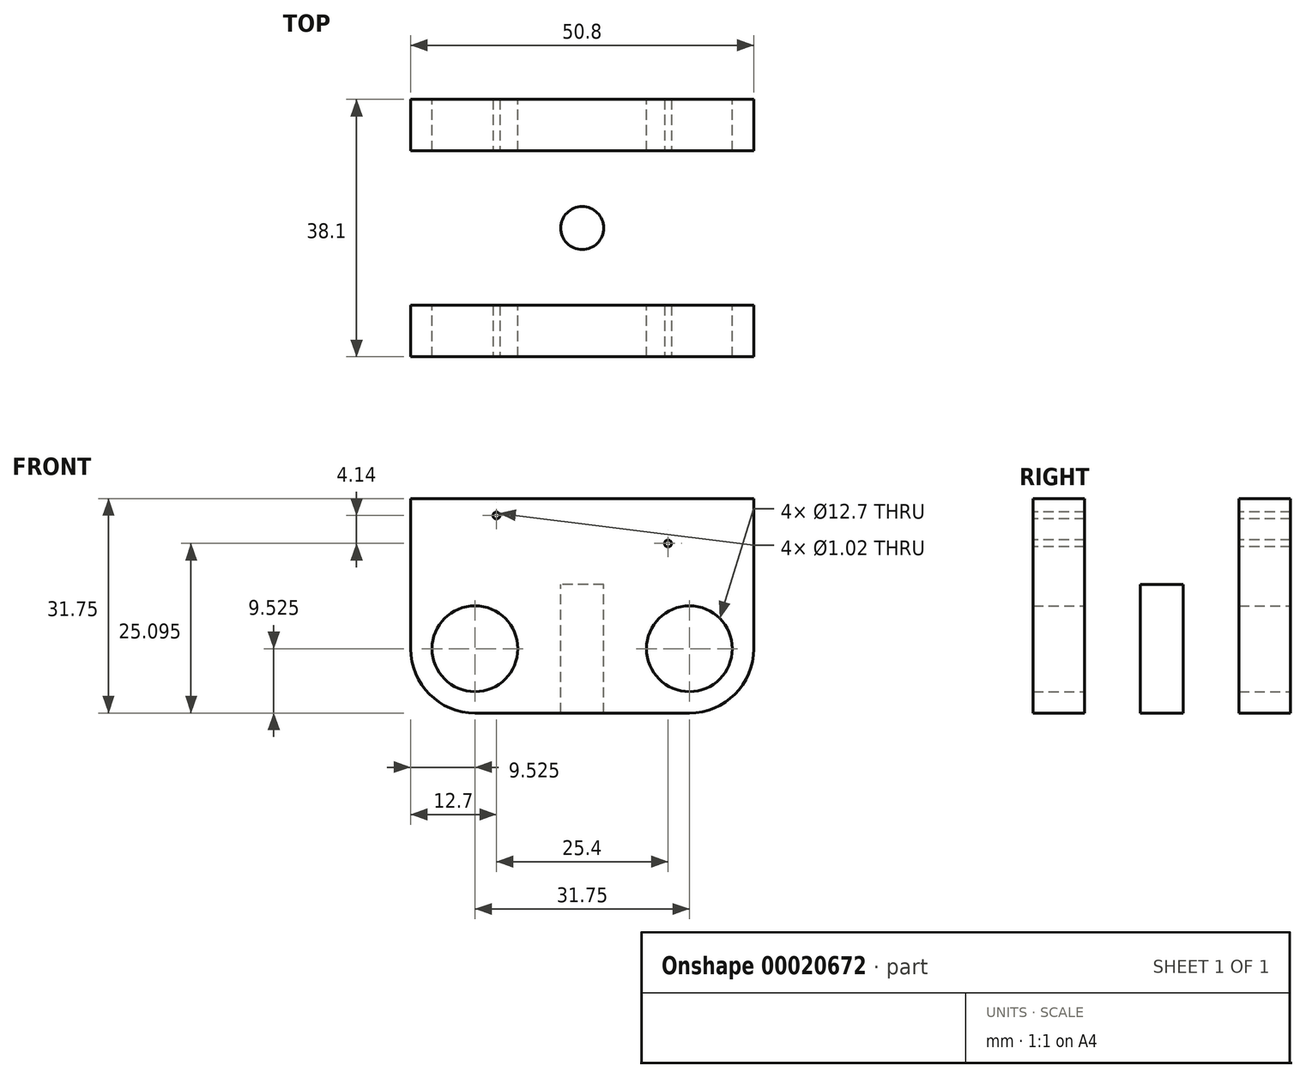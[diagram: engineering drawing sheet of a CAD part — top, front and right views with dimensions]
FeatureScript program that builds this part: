
annotation { "Feature Type Name" : "Feature", "Feature Type Description" : "" }
export const myFeature = defineFeature(function(context is Context, id is Id, definition is map)
    precondition{}
    {
        {
            var Q0;
            Q0=qCreatedBy(makeId("Front.planeOp"),FACE);
            var sketch = newSketch(context, id + "F0", { "sketchPlane" : qUnion([Q0])});
            skLineSegment(sketch, "E0.bottom", {"start": v(0, 0) * mm, "end": v(50.8, 0) * mm});
            skLineSegment(sketch, "E0.top", {"start": v(0, 19.05) * mm, "end": v(50.8, 19.05) * mm});
            skLineSegment(sketch, "E0.left", {"start": v(0, 0) * mm, "end": v(0, 19.05) * mm});
            skLineSegment(sketch, "E0.right", {"start": v(50.8, 0) * mm, "end": v(50.8, 19.05) * mm});
            skCircle(sketch, "E1", {"center": v(41.28, 9.52) * mm, "radius": 6.35 * mm});
            skCircle(sketch, "E2", {"center": v(9.53, 9.52) * mm, "radius": 6.35 * mm});
            skLineSegment(sketch, "E3", {"start": v(0, 9.52) * mm, "end": v(50.8, 9.52) * mm});
            skSolve(sketch);
        }
        {
            var Q0;
            {var subQ11=sQuery(id+"F0.wireOp",EDGE,"E0.top");Q0=makeQuery(id+"F0.imprint","IMPRINT",FACE,{"disambiguationData":[TD([[makeQuery(id+"F0.imprint","IMPRINT",EDGE,{"derivedFrom":subQ11}),-1.0]])]});}
            var Q1;
            {var subQ11=sQuery(id+"F0.wireOp",EDGE,"E0.bottom");Q1=makeQuery(id+"F0.imprint","IMPRINT",FACE,{"disambiguationData":[TD([[makeQuery(id+"F0.imprint","IMPRINT",EDGE,{"derivedFrom":subQ11}),1.0]])]});}
            extrude(context, id + "F1", {"entities" : qUnion([Q0, Q1]), "depth" : 38.1 * mm});
        }
        {
            var Q0;
            Q0=makeQuery(id+"F1.opExtrude","SWEPT_FACE",FACE,{"disambiguationData":[OSD([sQuery(id+"F0.wireOp",EDGE,"E0.top")])]});
            var sketch = newSketch(context, id + "F2", { "sketchPlane" : qUnion([Q0])});
            skLineSegment(sketch, "E4", {"start": v(25.4, -38.1) * mm, "end": v(25.4, 0) * mm});
            skCircle(sketch, "E5", {"center": v(25.4, -19.05) * mm, "radius": 3.18 * mm});
            skLineSegment(sketch, "E6.bottom", {"start": v(0, -30.48) * mm, "end": v(50.8, -30.48) * mm});
            skLineSegment(sketch, "E6.top", {"start": v(0, -38.1) * mm, "end": v(50.8, -38.1) * mm});
            skLineSegment(sketch, "E6.left", {"start": v(0, -30.48) * mm, "end": v(0, -38.1) * mm});
            skLineSegment(sketch, "E6.right", {"start": v(50.8, -30.48) * mm, "end": v(50.8, -38.1) * mm});
            skLineSegment(sketch, "E7", {"start": v(25.4, -19.05) * mm, "end": v(16.8, -19.05) * mm, "construction": true});
            skLineSegment(sketch, "E8.MirrorCS", {"start": v(50.8, -7.62) * mm, "end": v(50.8, 0) * mm});
            skLineSegment(sketch, "E9.MirrorCS", {"start": v(0, 0) * mm, "end": v(50.8, 0) * mm});
            skLineSegment(sketch, "E10.MirrorCS", {"start": v(0, -7.62) * mm, "end": v(0, 0) * mm});
            skLineSegment(sketch, "E11.MirrorCS", {"start": v(0, -7.62) * mm, "end": v(50.8, -7.62) * mm});
            skSolve(sketch);
        }
        {
            var Q0;
            {var subQ0=sQuery(id+"F2.wireOp",EDGE,"E5");var subQ1=sQuery(id+"F2.wireOp",EDGE,"E4");var subQ3=makeQuery(id+"F2.imprint","INTERSECT",VERTEX,{"disambiguationData":[OD(0.0)],"derivedFrom":[subQ1,subQ0]});Q0=makeQuery(id+"F2.imprint","IMPRINT",FACE,{"disambiguationData":[TD([[makeQuery(id+"F2.imprint","IMPRINT",EDGE,{"disambiguationData":[TD([[subQ3,-1.0]])],"derivedFrom":subQ1}),-1.0]])]});}
            var Q1;
            {var subQ0=sQuery(id+"F2.wireOp",EDGE,"E5");var subQ1=sQuery(id+"F2.wireOp",EDGE,"E4");var subQ3=makeQuery(id+"F2.imprint","INTERSECT",VERTEX,{"disambiguationData":[OD(0.0)],"derivedFrom":[subQ1,subQ0]});Q1=makeQuery(id+"F2.imprint","IMPRINT",FACE,{"disambiguationData":[TD([[makeQuery(id+"F2.imprint","IMPRINT",EDGE,{"disambiguationData":[TD([[subQ3,-1.0]])],"derivedFrom":subQ1}),1.0]])]});}
            var Q2;
            Q2=sQuery(id+"F2.wireOp",EDGE,"E5");
            extrude(context, id + "F3", {"entities" : qUnion([Q0, Q1]), "operationType" : NewBodyOperationType.REMOVE, "surfaceEntities" : qUnion([Q2]), "endBound" : BoundingType.THROUGH_ALL, "oppositeDirection" : true, "depth" : 25.4 * mm});
        }
        {
            var Q0;
            {var subQ0=sQuery(id+"F2.wireOp",EDGE,"E6.left");Q0=makeQuery(id+"F2.imprint","IMPRINT",FACE,{"disambiguationData":[TD([[makeQuery(id+"F2.imprint","IMPRINT",EDGE,{"derivedFrom":subQ0}),-1.0]])]});}
            var Q1;
            {var subQ0=sQuery(id+"F2.wireOp",EDGE,"E6.right");Q1=makeQuery(id+"F2.imprint","IMPRINT",FACE,{"disambiguationData":[TD([[makeQuery(id+"F2.imprint","IMPRINT",EDGE,{"derivedFrom":subQ0}),1.0]])]});}
            var Q2;
            {var subQ3=sQuery(id+"F2.wireOp",EDGE,"E10.MirrorCS");Q2=makeQuery(id+"F2.imprint","IMPRINT",FACE,{"disambiguationData":[TD([[makeQuery(id+"F2.imprint","IMPRINT",EDGE,{"derivedFrom":subQ3}),-1.0]])]});}
            var Q3;
            {var subQ3=sQuery(id+"F2.wireOp",EDGE,"E8.MirrorCS");Q3=makeQuery(id+"F2.imprint","IMPRINT",FACE,{"disambiguationData":[TD([[makeQuery(id+"F2.imprint","IMPRINT",EDGE,{"derivedFrom":subQ3}),1.0]])]});}
            extrude(context, id + "F4", {"entities" : qUnion([Q0, Q1, Q2, Q3]), "operationType" : NewBodyOperationType.ADD, "depth" : 12.7 * mm});
        }
        {
            var Q0;
            Q0=makeQuery(id+"F4.boolean.opBoolean","MERGE",FACE,{"derivedFrom":[makeQuery(id+"F1.opExtrude","CAP_FACE",FACE,{"disambiguationData":[OSD([sQuery(id+"F0.wireOp",EDGE,"E0.bottom"),sQuery(id+"F0.wireOp",EDGE,"E0.top"),sQuery(id+"F0.wireOp",EDGE,"E0.left"),sQuery(id+"F0.wireOp",EDGE,"E0.right"),sQuery(id+"F0.wireOp",EDGE,"E1"),sQuery(id+"F0.wireOp",EDGE,"E2")])],"isStart":false}),makeQuery(id+"F4.opExtrude","SWEPT_FACE",FACE,{"disambiguationData":[OSD([sQuery(id+"F2.wireOp",EDGE,"E6.top")])]})]});
            var sketch = newSketch(context, id + "F5", { "sketchPlane" : qUnion([Q0])});
            skCircle(sketch, "E12", {"center": v(38.1, 25.1) * mm, "radius": 0.5 * mm});
            skCircle(sketch, "E13", {"center": v(12.7, 29.24) * mm, "radius": 0.5 * mm});
            skLineSegment(sketch, "E14", {"start": v(25.4, 31.75) * mm, "end": v(25.4, 0) * mm});
            skSolve(sketch);
        }
        {
            var Q0;
            Q0 = qSketchRegion(id + "F5", true);
            extrude(context, id + "F6", {"entities" : qUnion([Q0]), "operationType" : NewBodyOperationType.REMOVE, "endBound" : BoundingType.THROUGH_ALL, "oppositeDirection" : true, "depth" : 25.4 * mm});
        }
        {
            var Q0;
            Q0=makeQuery(id+"F1.opExtrude","SWEPT_EDGE",EDGE,{"disambiguationData":[OSD([sQuery(id+"F0.wireOp",EDGE,"E0.top"),sQuery(id+"F0.wireOp",EDGE,"E0.right")])]});
            var Q1;
            Q1=makeQuery(id+"F1.opExtrude","SWEPT_EDGE",EDGE,{"disambiguationData":[OSD([sQuery(id+"F0.wireOp",EDGE,"E0.bottom"),sQuery(id+"F0.wireOp",EDGE,"E0.right")])]});
            var Q2;
            Q2=makeQuery(id+"F1.opExtrude","SWEPT_EDGE",EDGE,{"disambiguationData":[OSD([sQuery(id+"F0.wireOp",EDGE,"E0.top"),sQuery(id+"F0.wireOp",EDGE,"E0.left")])]});
            var Q3;
            Q3=makeQuery(id+"F1.opExtrude","SWEPT_EDGE",EDGE,{"disambiguationData":[OSD([sQuery(id+"F0.wireOp",EDGE,"E0.bottom"),sQuery(id+"F0.wireOp",EDGE,"E0.left")])]});
            fillet(context, id + "F7", {"entities" : qUnion([Q0, Q1, Q2, Q3]), "radius" : 9.52 * mm, "tangentPropagation" : true, "allowEdgeOverflow" : false});
        }
    });
